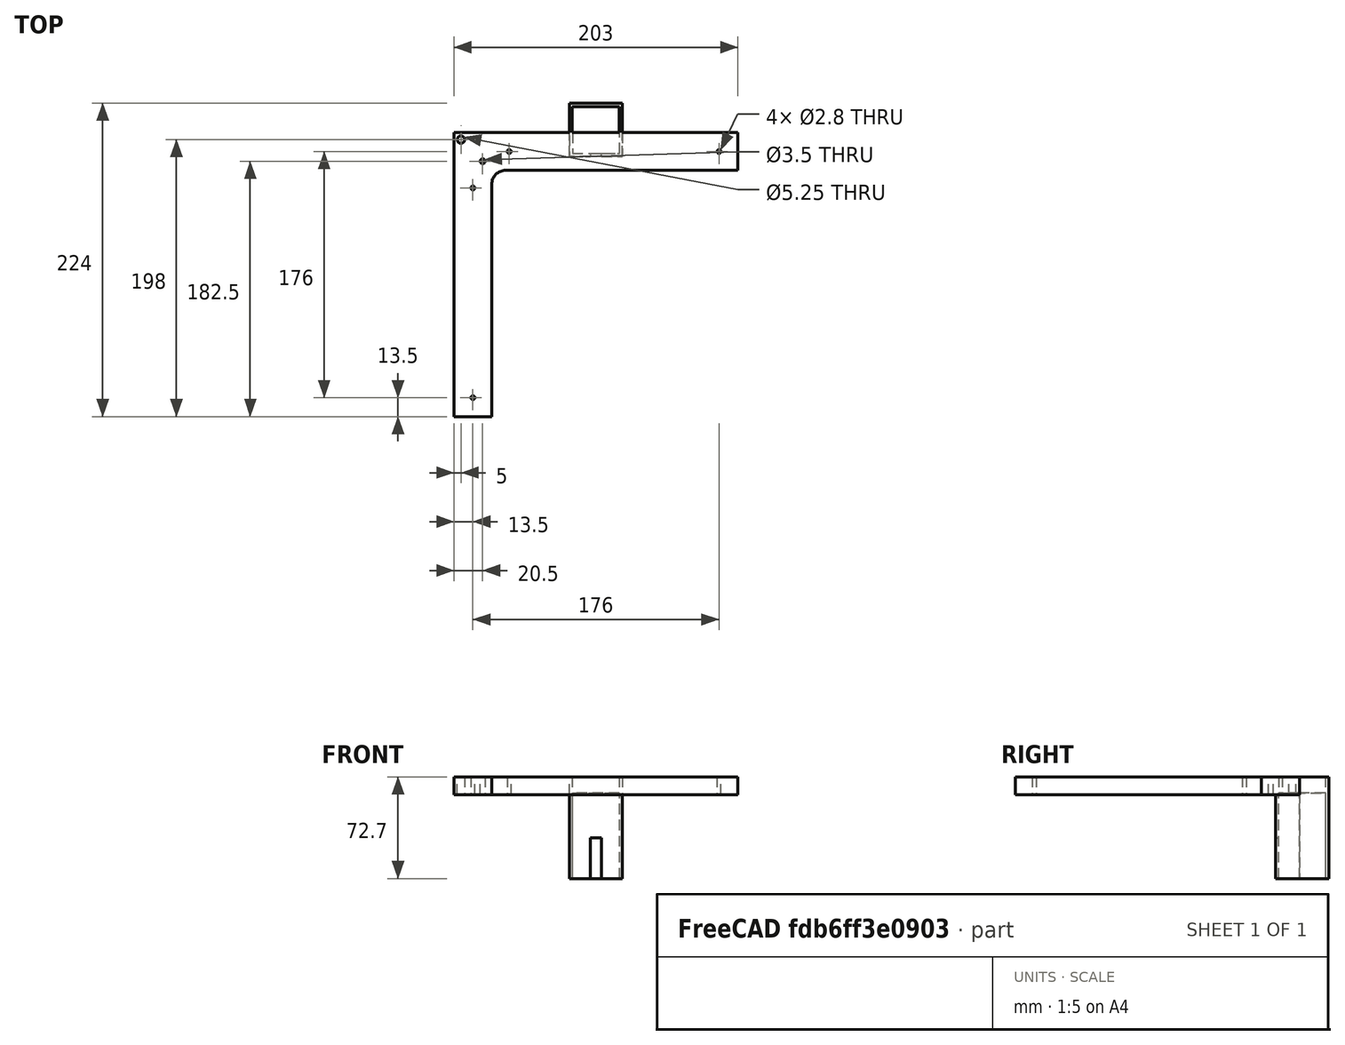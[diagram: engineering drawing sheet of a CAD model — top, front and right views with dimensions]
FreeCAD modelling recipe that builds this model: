
FCSTD DOCUMENT  (FreeCAD 0.19R)
Label: L
License: All rights reserved
LicenseURL: http://en.wikipedia.org/wiki/All_rights_reserved
objects: Sketcher::SketchObject×9, PartDesign::Pocket×7, PartDesign::Pad×2, PartDesign::Fillet×1, PartDesign::Body×1, Mesh::Feature×1
note: 30 computed .brp shape members not serialized (recipe doc carries the construction recipe); baked Part::Feature solids carry a one-line shape summary decoded from their .brp

FEATURE [Sketcher::SketchObject] Sketch
  FullyConstrained = true
  MapMode = 5
  Support = -> [XY_Plane]
  sketch-geometry (4):
    g0: LineSegment StartX=-101.5 StartY=101.5 StartZ=0 EndX=101.5 EndY=101.5 EndZ=0
    g1: LineSegment StartX=101.5 StartY=101.5 StartZ=0 EndX=101.5 EndY=-101.5 EndZ=0
    g2: LineSegment StartX=101.5 StartY=-101.5 StartZ=0 EndX=-101.5 EndY=-101.5 EndZ=0
    g3: LineSegment StartX=-101.5 StartY=-101.5 StartZ=0 EndX=-101.5 EndY=101.5 EndZ=0
  constraints (11):
    c: Coincident(g0,g1)
    c: Coincident(g1,g2)
    c: Coincident(g2,g3)
    c: Coincident(g3,g0)
    c: Horizontal(g0)
    c: Horizontal(g2)
    c: Vertical(g1)
    c: Vertical(g3)
    c: Equal(g3,g0)
    c: Symmetric(g0,g1,g-1)
    c: Distance(g0) = 203
FEATURE [PartDesign::Pad] Pad
  Direction = (1,1,1)
  Length = 12.7
  Length2 = 100
  Profile = -> Sketch
  Type = 0
FEATURE [Sketcher::SketchObject] Sketch001
  ExternalGeometry = -> [Pad]
  FullyConstrained = false
  MapMode = 5
  Placement = pos=(0,0,12.7) rot=(0,0,1;0rad)
  Support = -> [Pad]
  sketch-geometry (4):
    g0: LineSegment StartX=-74.5 StartY=74.5 StartZ=0 EndX=115.786 EndY=74.5 EndZ=0
    g1: LineSegment StartX=115.786 StartY=74.5 StartZ=0 EndX=115.786 EndY=-105.664 EndZ=0
    g2: LineSegment StartX=115.786 StartY=-105.664 StartZ=0 EndX=-74.5 EndY=-105.664 EndZ=0
    g3: LineSegment StartX=-74.5 StartY=-105.664 StartZ=0 EndX=-74.5 EndY=74.5 EndZ=0
  constraints (10):
    c: Coincident(g0,g1)
    c: Coincident(g1,g2)
    c: Coincident(g2,g3)
    c: Coincident(g3,g0)
    c: Horizontal(g0)
    c: Horizontal(g2)
    c: Vertical(g1)
    c: Vertical(g3)
    c: Distance(g-3,g3) = 27
    c: DistanceY(g0,g-3) = 27
FEATURE [PartDesign::Pocket] Pocket
  BaseFeature = -> Pad
  Length = 5
  Length2 = 100
  Profile = -> Sketch001
  Type = 1
FEATURE [Sketcher::SketchObject] Sketch002
  ExternalGeometry = -> [Pocket]
  FullyConstrained = true
  MapMode = 5
  Placement = pos=(0,0,0) rot=(1,0,0;3.14159rad)
  Support = -> [Pocket]
  sketch-geometry (4):
    g0: LineSegment StartX=-19 StartY=-84.5 StartZ=0 EndX=19 EndY=-84.5 EndZ=0
    g1: LineSegment StartX=19 StartY=-84.5 StartZ=0 EndX=19 EndY=-122.5 EndZ=0
    g2: LineSegment StartX=19 StartY=-122.5 StartZ=0 EndX=-19 EndY=-122.5 EndZ=0
    g3: LineSegment StartX=-19 StartY=-122.5 StartZ=0 EndX=-19 EndY=-84.5 EndZ=0
  constraints (11):
    c: Coincident(g0,g1)
    c: Coincident(g1,g2)
    c: Coincident(g2,g3)
    c: Coincident(g3,g0)
    c: Horizontal(g2)
    c: Vertical(g1)
    c: Vertical(g3)
    c: Symmetric(g0,g0,g-2)
    c: Equal(g0,g1)
    c: Distance(g1) = 38
    c: Distance(g0,g-3) = 10
FEATURE [PartDesign::Pad] Pad001
  BaseFeature = -> Pocket
  Direction = (1,1,1)
  Length = 60
  Length2 = 12.7
  Profile = -> Sketch002
  Type = 4
FEATURE [Sketcher::SketchObject] Sketch004
  FullyConstrained = false
  MapMode = 5
  Placement = pos=(0,0,0) rot=(1,0,0;3.14159rad)
  sketch-geometry (4):
    g0: Circle CenterX=88 CenterY=-88 CenterZ=0 NormalX=0 NormalY=0 NormalZ=1 AngleXU=0 Radius=1.4
    g1: Circle CenterX=-62 CenterY=-88 CenterZ=0 NormalX=0 NormalY=0 NormalZ=1 AngleXU=0 Radius=1.4
    g2: Circle CenterX=-88 CenterY=-62 CenterZ=0 NormalX=0 NormalY=0 NormalZ=1 AngleXU=0 Radius=1.4
    g3: Circle CenterX=-88 CenterY=88 CenterZ=0 NormalX=0 NormalY=0 NormalZ=1 AngleXU=0 Radius=1.4
  constraints (6):
    c: Distance(g0,g1) = 150
    c: Distance(g2,g3) = 150
    c: Diameter(g0) = 2.8
    c: Equal(g0,g1)
    c: Equal(g0,g2)
    c: Equal(g0,g3)
FEATURE [Sketcher::SketchObject] Sketch005
  FullyConstrained = false
  MapMode = 5
  Placement = pos=(0,0,12.7) rot=(0,0,1;0rad)
  sketch-geometry (1):
    g0: Circle CenterX=-96.5 CenterY=96.5 CenterZ=0 NormalX=0 NormalY=0 NormalZ=1 AngleXU=0 Radius=2.62435
FEATURE [PartDesign::Pocket] Pocket001
  BaseFeature = -> Pad001
  Length = 5
  Length2 = 100
  Profile = -> Sketch004
  Type = 1
FEATURE [PartDesign::Pocket] Pocket002
  BaseFeature = -> Pocket001
  Length = 5
  Length2 = 100
  Profile = -> Sketch005
  Type = 1
FEATURE [Sketcher::SketchObject] Sketch006
  ExternalGeometry = -> [Pocket002]
  FullyConstrained = true
  MapMode = 5
  Placement = pos=(0,0,12.7) rot=(0,0,1;0rad)
  sketch-geometry (1):
    g0: Circle CenterX=-81 CenterY=81 CenterZ=0 NormalX=0 NormalY=0 NormalZ=1 AngleXU=0 Radius=1.75
  constraints (3):
    c: DistanceX(g-3,g0) = 15.5
    c: DistanceY(g0,g-3) = 15.5
    c: Diameter(g0) = 3.5
FEATURE [PartDesign::Pocket] Pocket003
  BaseFeature = -> Pocket002
  Length = 5
  Length2 = 100
  Profile = -> Sketch006
  Type = 1
FEATURE [Sketcher::SketchObject] Sketch007
  FullyConstrained = false
  MapMode = 5
  Placement = pos=(0,0,-60) rot=(1,0,0;3.14159rad)
  Support = -> [Pocket003]
  sketch-geometry (4):
    g0: LineSegment StartX=-16.8 StartY=-86.6618 StartZ=0 EndX=16.8 EndY=-86.6618 EndZ=0
    g1: LineSegment StartX=16.8 StartY=-86.6618 StartZ=0 EndX=16.8 EndY=-120.262 EndZ=0
    g2: LineSegment StartX=16.8 StartY=-120.262 StartZ=0 EndX=-16.8 EndY=-120.262 EndZ=0
    g3: LineSegment StartX=-16.8 StartY=-120.262 StartZ=0 EndX=-16.8 EndY=-86.6618 EndZ=0
  constraints (10):
    c: Coincident(g0,g1)
    c: Coincident(g1,g2)
    c: Coincident(g2,g3)
    c: Coincident(g3,g0)
    c: Horizontal(g2)
    c: Vertical(g1)
    c: Vertical(g3)
    c: Symmetric(g0,g0,g-2)
    c: Distance(g0) = 33.6
    c: Distance(g1) = 33.6
FEATURE [PartDesign::Pocket] Pocket004
  BaseFeature = -> Pocket003
  Length = 61
  Length2 = 100
  Profile = -> Sketch007
  Type = 0
FEATURE [Sketcher::SketchObject] Sketch008
  FullyConstrained = false
  MapMode = 5
  Placement = pos=(0,0,12.7) rot=(0,0,1;0rad)
  Support = -> [Pocket004]
  sketch-geometry (4):
    g0: LineSegment StartX=-16.9132 StartY=120.054 StartZ=0 EndX=16.6868 EndY=120.054 EndZ=0
    g1: LineSegment StartX=16.6868 StartY=120.054 StartZ=0 EndX=16.6868 EndY=101.501 EndZ=0
    g2: LineSegment StartX=16.6868 StartY=101.501 StartZ=0 EndX=-16.9132 EndY=101.501 EndZ=0
    g3: LineSegment StartX=-16.9132 StartY=101.501 StartZ=0 EndX=-16.9132 EndY=120.054 EndZ=0
  constraints (9):
    c: Coincident(g0,g1)
    c: Coincident(g1,g2)
    c: Coincident(g2,g3)
    c: Coincident(g3,g0)
    c: Horizontal(g0)
    c: Horizontal(g2)
    c: Vertical(g1)
    c: Vertical(g3)
    c: Distance(g0) = 33.6
FEATURE [PartDesign::Pocket] Pocket005
  BaseFeature = -> Pocket004
  Length = 5
  Length2 = 100
  Profile = -> Sketch008
  Type = 1
FEATURE [PartDesign::Fillet] Fillet
  Base = -> Pocket005 [Edge41]
  BaseFeature = -> Pocket005
  Radius = 10
  SupportTransform = false
FEATURE [Sketcher::SketchObject] Sketch009
  FullyConstrained = false
  MapMode = 5
  Placement = pos=(0,0,-60) rot=(1,0,0;3.14159rad)
  Support = -> [Fillet]
  sketch-geometry (4):
    g0: LineSegment StartX=-4 StartY=-81.0938 StartZ=0 EndX=4 EndY=-81.0938 EndZ=0
    g1: LineSegment StartX=4 StartY=-81.0938 StartZ=0 EndX=4 EndY=-99.4003 EndZ=0
    g2: LineSegment StartX=4 StartY=-99.4003 StartZ=0 EndX=-4 EndY=-99.4003 EndZ=0
    g3: LineSegment StartX=-4 StartY=-99.4003 StartZ=0 EndX=-4 EndY=-81.0938 EndZ=0
  constraints (9):
    c: Coincident(g0,g1)
    c: Coincident(g1,g2)
    c: Coincident(g2,g3)
    c: Coincident(g3,g0)
    c: Horizontal(g0)
    c: Vertical(g1)
    c: Vertical(g3)
    c: Symmetric(g1,g2,g-2)
    c: Distance(g0) = 8
FEATURE [PartDesign::Pocket] Pocket006
  BaseFeature = -> Fillet
  Length = 29
  Length2 = 100
  Profile = -> Sketch009
  Type = 0
FEATURE [PartDesign::Body] Body
  Group = -> [Sketch,Pad,Sketch001,Pocket,Sketch002,Pad001,Sketch004,Sketch005,Sketch006,Pocket001,Pocket002,Pocket003,Sketch007,Pocket004,Sketch008,Pocket005,Fillet,Sketch009,Pocket006]
  Origin = -> Origin
  Tip = -> Pocket006
FEATURE [Mesh::Feature] Mesh  label="Pocket006 (Meshed)"
